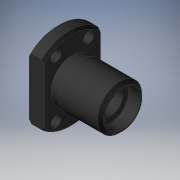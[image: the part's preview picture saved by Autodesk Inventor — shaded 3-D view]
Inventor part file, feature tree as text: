
AUTODESK INVENTOR PART (.ipt)
format: ipt  version: 2019 (Build 230136000, 136)  size: 196,608 bytes
history: native  units: mm
features: sketch x11, other x7, hole x5, extrude x3, revolve x3
ambient origin geometry x8: Origin, YZ Plane, XZ Plane, XY Plane, X Axis, Y Axis, Z Axis, Center Point
bodies: Solid1 (feature_tree)
feature tree (29):
  extrude  "Extrusion1"  TaperAngle=360.0deg  [1 undecoded]
  revolve  "Revolution1"  Angle=360.0deg
  revolve  "Revolution2"  [1 undecoded]
  hole  "Hole1"  [1 undecoded]
  hole  "Hole2"  [1 undecoded]
  hole  "Hole3"  [1 undecoded]
  hole  "Hole4"  [1 undecoded]
  hole  "Hole5"  [1 undecoded]
  revolve  "Revolution3"  [1 undecoded]
  extrude  "Extrusion2"  [1 undecoded]
  extrude  "Extrusion3"  [1 undecoded]
  other  "mdk_2_XY"
  other  "mdk_2_YZ"
  other  "mdk_2_ZX"
  other  "mdk_2_X"
  other  "mdk_2_Y"
  other  "mdk_2_Z"
  other  "mdk_2_Center"
  sketch  "Sketch_1"  dims[d0=5.0mm d1=0.0mm d2=360.0deg]
  sketch  "Sketch_9"  dims[d44=0.0mm]
  sketch  "Sketch_10"
  sketch  "Sketch4"  dims[d3=360.0deg]
  sketch  "Sketch5"  dims[d4=3.4mm d5=6.0mm d6=4.0mm d7=2.0mm d8=90.0deg d9=5.0mm d10=0.0mm]
  sketch  "Sketch6"  dims[d18=3.4mm d19=6.0mm d20=4.0mm d21=2.0mm d22=90.0deg d23=5.0mm d24=0.0mm]
  sketch  "Sketch7"  dims[d32=8.0mm d33=6.0mm d34=4.0mm d35=2.0mm d36=90.0deg d37=5.0mm d38=0.0mm d39=360.0deg]
  sketch  "Sketch8"  dims[d40=4.0mm d41=0.0mm d42=4.0mm d43=0.0mm]
  sketch  "Sketch_14"
  sketch  "Sketch_5"  dims[d11=3.4mm d12=6.0mm d13=4.0mm d14=2.0mm d15=90.0deg d16=5.0mm d17=0.0mm]
  sketch  "Sketch_6"  dims[d25=3.4mm d26=6.0mm d27=4.0mm d28=2.0mm d29=90.0deg d30=5.0mm d31=0.0mm]
note: 10 required parameter values undecoded (feature->parameter linkage not recoverable at this tier; creation-order binding heuristic only, values carry confidence <= 0.55)